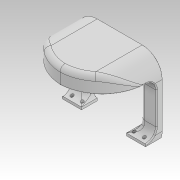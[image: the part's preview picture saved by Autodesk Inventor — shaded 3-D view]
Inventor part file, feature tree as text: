
AUTODESK INVENTOR PART (.ipt)
format: ipt  version: 2020 (Build 240168000, 168)  size: 1,174,528 bytes
history: native  units: mm
features: sketch x16, extrude x14, projected_geometry x6, fillet x4, plane x4, mirror x2, other x2, chamfer x2, revolve x1
ambient origin geometry x8: Origin, YZ Plane, XZ Plane, XY Plane, X Axis, Y Axis, Z Axis, Center Point
bodies: Solid1 (feature_tree)
feature tree (51):
  extrude  "Extrusion1"  Depth=170.0mm
  extrude  "Extrusion2"  Depth=33.0mm
  extrude  "Extrusion3"  Depth=12.0mm
  sketch  "Sketch4"  dims[d8=20.0mm d9=0.0mm d10=0.0mm]
  revolve  "Revolution1"  [1 undecoded]
  extrude  "Extrusion4"  Depth=47.55mm
  extrude  "Extrusion5"  Depth=3.0mm
  fillet  "Fillet1"  Radius=1.0mm
  extrude  "Extrusion8"  Depth=17.5mm
  mirror  "Mirror1"
  extrude  "Extrusion6"  TaperAngle=90.0deg  [1 undecoded]
  extrude  "Extrusion7"  Depth=0.6mm
  extrude  "Extrusion9"  Depth=5.2mm
  other  "Spur Gear Teeth1"
  extrude  "Extrusion10"  Depth=1.0mm
  extrude  "Extrusion11"  Depth=25.0mm
  mirror  "Mirror2"
  fillet  "Fillet3"  Radius=19.0mm
  plane  "Work Plane2"
  extrude  "Extrusion12"  Depth=15.0mm
  extrude  "Extrusion13"  Depth=104.0mm
  plane  "Work Plane3"
  sketch  "Sketch15"  dims[d37=8.0mm d38=45.0deg d39=6.4mm d40=40.0mm d42=360.0deg d44=12.5mm d45=0.0mm]
  plane  "Work Plane4"
  extrude  "Extrusion14"  TaperAngle=45.0deg  [1 undecoded]
  fillet  "Fillet4"  Radius=6.4mm
  fillet  "Fillet5"  Radius=40.0mm
  chamfer  "Chamfer1"  Distance=12.5mm
  chamfer  "Chamfer2"  Distance=5.0mm
  sketch  "Sketch1"  dims[d0=170.0mm d1=170.0mm]
  sketch  "Sketch2"  dims[d2=40.0mm d3=33.0mm]
  projected_geometry  "Projected Loop1"
  projected_geometry  "Projected Loop2"
  sketch  "Sketch3"  dims[d4=120.0mm d5=0.0mm d7=12.0mm]
  projected_geometry  "Projected Loop3"
  sketch  "Sketch5"  dims[d11=0.0mm d12=0.0mm d13=47.55mm]
  sketch  "Sketch6"  dims[d14=10.1mm d15=3.0mm d16=1.0mm]
  projected_geometry  "Projected Loop4"
  sketch  "Sketch7"  dims[d17=40.075mm d18=17.5mm]
  sketch  "Sketch8"  dims[d19=65.0mm d20=90.0deg]
  sketch  "Sketch9"  dims[d21=8.05mm d22=0.6mm]
  sketch  "Sketch10"  dims[d23=1.5mm d25=5.2mm]
  other  "Spur Gear2"
  sketch  "Sketch11"  dims[d26=1.0mm d27=1.0mm]
  projected_geometry  "Projected Loop5"
  sketch  "Sketch12"  dims[d29=25.0mm d30=2.0mm d31=19.0mm]
  plane  "Work Plane1"
  sketch  "Sketch13"  dims[d32=38.0mm d33=15.0mm]
  sketch  "Sketch14"  dims[d34=5.0mm d35=0.0mm d36=104.0mm]
  projected_geometry  "Projected Loop6"
  sketch  "Sketch16"  dims[d46=10.0mm d47=5.0mm d48=0.0mm d49=137.0mm d50=0.0mm d51=3.7mm d52=12.0mm d53=7.0mm d54=5.0mm d55=17.0mm d56=0.0mm d57=0.0mm d58=35.0mm d59=72.5mm d60=5.0mm d61=0.0mm d62=75.0mm d63=5.0mm d64=0.0mm d65=5.0mm d66=0.0mm d67=16.0mm d69=10.0mm d70=-2.5mm d71=6.0mm d72=42.0mm d73=0.0mm d74=75.0mm d75=5.0mm d76=92.0mm d77=8.0mm d78=0.0mm d79=12.0mm d80=4.363323mm d81=15.0mm d82=6.4mm d83=51.5mm d84=0.0mm d85=0.5mm d86=2.0mm d87=0.5mm d88=2.0mm d89=45.0deg d90=60.0deg d91=9.599311mm d92=9.599311mm d93=0.5mm d94=2.0mm d95=45.0deg]
note: 3 required parameter values undecoded (feature->parameter linkage not recoverable at this tier; creation-order binding heuristic only, values carry confidence <= 0.55)